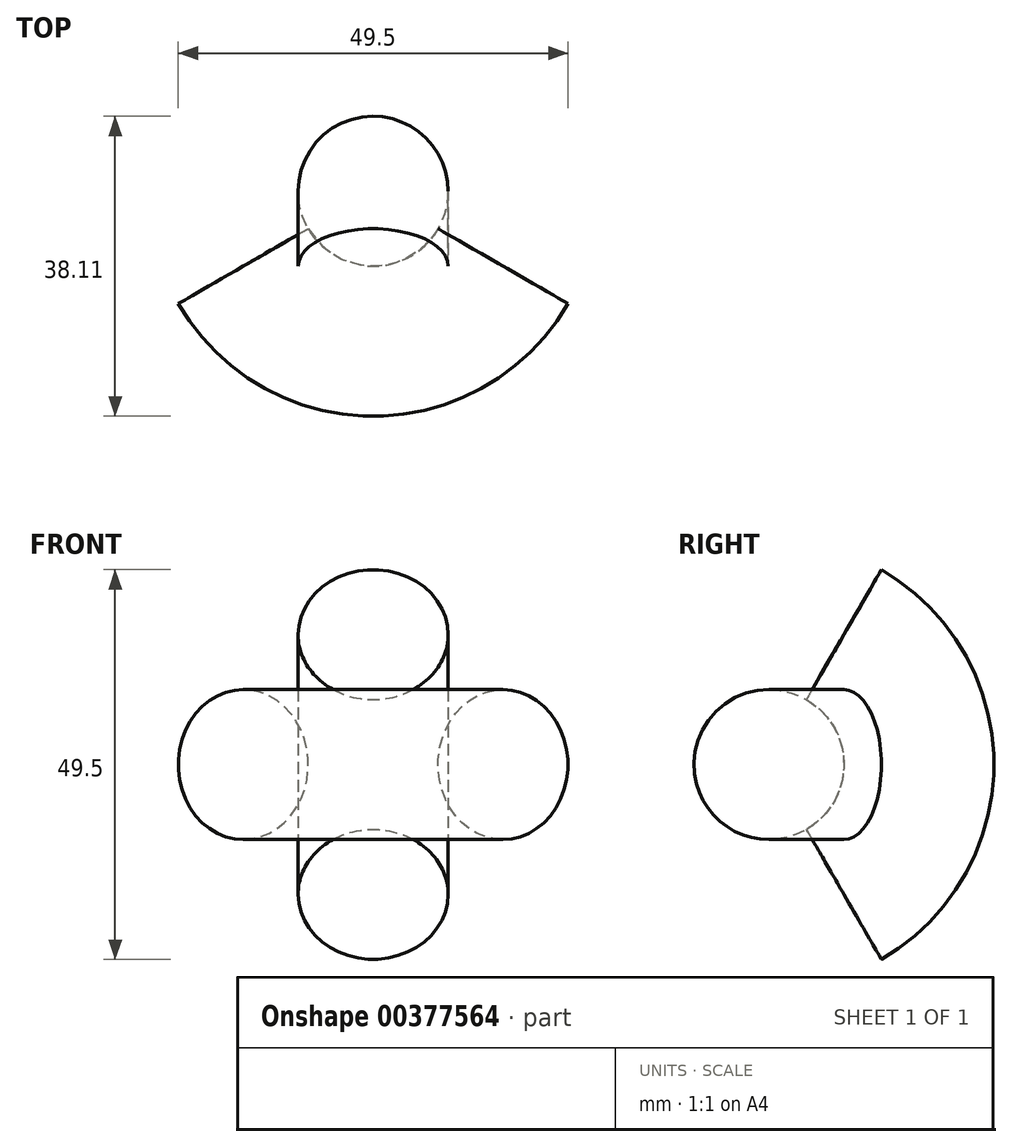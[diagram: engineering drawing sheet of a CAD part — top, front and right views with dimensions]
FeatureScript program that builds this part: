
annotation { "Feature Type Name" : "Feature", "Feature Type Description" : "" }
export const myFeature = defineFeature(function(context is Context, id is Id, definition is map)
    precondition{}
    {
        {
            var Q0;
            Q0=qCreatedBy(makeId("Right.planeOp"),FACE);
            var sketch = newSketch(context, id + "F0", { "sketchPlane" : qUnion([Q0])});
            skCircle(sketch, "E0", {"center": v(-19.05, 0) * mm, "radius": 9.53 * mm});
            skLineSegment(sketch, "E1", {"start": v(0, 41.51) * mm, "end": v(0, -24.28) * mm});
            skSolve(sketch);
        }
        {
            var Q0;
            Q0=makeQuery(id+"F0.imprint","IMPRINT",FACE,{"disambiguationData":[TD([[makeQuery(id+"F0.imprint","IMPRINT",EDGE,{"derivedFrom":sQuery(id+"F0.wireOp",EDGE,"E0")}),1.0]])]});
            var Q1;
            Q1=sQuery(id+"F0.wireOp",EDGE,"E1");
            revolve(context, id + "F1", {"entities" : qUnion([Q0]), "axis" : qUnion([Q1]), "revolveType" : RevolveType.TWO_DIRECTIONS, "angle" : 60 * degree, "angleBack" : 300 * degree});
        }
        {
            var Q0;
            Q0=qCreatedBy(makeId("Top.planeOp"),FACE);
            var sketch = newSketch(context, id + "F2", { "sketchPlane" : qUnion([Q0])});
            skCircle(sketch, "E2", {"center": v(0, 0) * mm, "radius": 9.53 * mm});
            skLineSegment(sketch, "E3", {"start": v(-12.64, -19.05) * mm, "end": v(31.31, -19.05) * mm});
            skSolve(sketch);
        }
        {
            var Q0;
            Q0 = qSketchRegion(id + "F2", true);
            var Q1;
            Q1=sQuery(id+"F2.wireOp",EDGE,"E3");
            revolve(context, id + "F3", {"operationType" : NewBodyOperationType.ADD, "entities" : qUnion([Q0]), "axis" : qUnion([Q1]), "revolveType" : RevolveType.TWO_DIRECTIONS, "angle" : 60 * degree, "angleBack" : 300 * degree});
        }
    });
